# Revit family: Paper_Towel_Dispenser_Waste_Receptacle-Bobrick-TrimLineSeries-B-38032
name_source: partatom
category: Specialty Equipment
revit_build: Autodesk Revit 2018 (Build: 20170223_1515(x64)
units: mm (PartAtom-declared; Revit-internal decimal feet)

## family parameters
Cut with Voids When Loaded = No
Host = Face
OmniClass Number = 23.40.20.21.17
OmniClass Title = Paper Towel Dispensers, Disposal Units
Part Type = Normal
Room Calculation Point = No
Round Connector Dimension = Use Diameter
Shared = Yes

## types (1)
- B-38032
    3803-130 Towel Mate = Yes
    ADA = Yes
    ADA Compliant = Yes
    Assembly Code = C1030200
    Cabinet Material = Metal-Bobrick-Stainless Steel
    Default Elevation = 0"
    Depth = 6 3/16"
    Description = TrimLineSeries Paper Towel Dispenser And Waste Receptacle
    Door Material = Stainless Steel-Bobrick-Satin
    Height = 55 1/8"
    Installation Type = Rcessed Wall Mounted
    Manufacturer = Bobrick
    Material = Stainless Steel-Bobrick-Satin
    Model = B-38032
    Mounting Height = 59 3/4"
    Mounting Height Constraint = 59 3/4"
    Paper Towel Dispenser Material = Stainless Steel-Bobrick-Satin
    Product Documentation Link = https://www.bobrick.com
    Product Page URL = https://www.bobrick.com
    Revised Date = 10/15/2021
    Rough Wall Opening Depth = 3 3/4"
    Rough Wall Opening Height = 53 5/8"
    Rough Wall Opening Width = 11 1/2"
    Skirt Material = Stainless Steel-Bobrick-Satin
    TowelMate Towel Rod Assembly Material = Nylon-Bobrick
    Type Comments = Dispenses 600 C-fold, 800 multifold or 1100 single fold towels.
    URL = http://www.bobrick.com
    Waste Capacity = 6.3-gal. (24-L)
    Waste Container Material = Plastic-Bobrick
    Width = 13"

## geometry (parser evidence)
native form markers: Sweep x3
no freeform markers — native parametric forms only
